# Revit family: Grohe_ThermostaticShowerMixer_34827KF0
name_source: partatom
category: Plumbing Fixtures
units: mm (PartAtom-declared; Revit-internal decimal feet)

## family parameters
Cut with Voids When Loaded = No
Host = Face
OmniClass Number = 23.45.05.00
OmniClass Title = Sanitary Equipment
Part Type = Normal
Room Calculation Point = No
Round Connector Dimension = Use Diameter
Shared = No

## types (1)
- Thermostatic Shower Mixer (34827KF0)
    Assembly Code = D2013
    AssetType = Fixed
    BIMObjectName = Grohe_ThermostaticShowerMixer_34827KF0
    CO2NeutralProduction = GROHE is one of the first leading manufacturer within the sanitary industry having a CO2-neutral production.
    ClassificationName = Uniclass2015
    ClassificationValue = Pr_40_20_87_55
    Color = Grohe_Black
    Cost = 0 $
    Default Elevation = 0 mm  [stored 0 ft]
    Description = Thermostatic Shower Mixer
    DimensionsDocumentLink = https://cdn.cloud.grohe.com
    DocumentationCertificates = https://www.bimstore.co
    DocumentationInstallationGuide = https://www.bimstore.co
    DocumentationLiterature = https://www.bimstore.co
    DocumentationMaintenance = https://www.bimstore.co
    DocumentationTechnical = https://www.bimstore.co
    DurationUnit = Years
    Ecojoy = No
    ExpectedLife = 0
    Finish = Black
    FullRecyclabilityOfPlastic = All plastic components are fully recycable
    GROHESocialCommittment = green.grohe.com/social_engagement
    GROHESustainability = green.grohe.com
    IfcExportAs = IfcPipeFitting
    IfcExportType = IfcPipeFittingType
    Keynote = N16
    Manufacturer = Grohe
    ManufacturerName = Grohe
    Model = Thermostatic Shower Mixer
    ModelNumber = 34827KF0
    ModelReference = Thermostatic Shower Mixer
    NBSDescription = Shower fittings package
    NBSObjectName = Grohe - Shower fittings package
    NBSReference = 45-35-70/323
    NominalDepth = 0 mm  [stored 0 ft]
    NominalHeight = 0 mm  [stored 0 ft]
    NominalLength = 0 mm  [stored 0 ft]
    PQDiagramLink = https://cdn.cloud.grohe.com
    PrimaryMaterial = Grohe_Black
    ProductDescription = wall mounted

GROHE CoolTouch safety housing

GROHE Long-Life finish

GROHE SafeStop safety button at 38°C

GROHE SafeStop Plus optional temperature limiter at 43°C included

GROHE TurboStat compact cartridge with wax thermoelement

GROHE ProGrip with knurl structure

integrated mixed water shut off

volume handle with GROHE EcoButton (economy button with individually adjustable economy stop)

ceramic headpart 1/2", 180°

shower bottom outlet 1/2"

built-in non return valves

dirt strainers

protected against backflow

S-unions

metal escutcheon

GROHE Water Saving - Less water, perfect flow

professional exclusive
    ProductNumber = 34827KF0
    ProductShortText = Thermostatic shower mixer 1/2"
    ProductType = Thermostat
    ProductionYear = 2023
    SustainabilityAward = green.grohe.com/awards
    SustainabilityReport = green.grohe.com/reporting
    TPIDocumentLink = https://cdn.cloud.grohe.com
    Type Comments = Thermostatic Shower Mixer
    TypeName = Thermostatic Shower Mixer
    URL = https://www.grohe.co.uk
    WarrantyDurationLabor = 0
    WarrantyDurationParts = 0
    WarrantyDurationUnit = Years
    _BSBibleVersion = 17
    _BimSpecGuid = 0
    _CurrentRevision = 1
    _DistributedBy = https://www.bimstore.co
    _ObjectUserGuide = https://www.bimstore.co

note: [stored X ft] marks values corroborated as IEEE doubles in the binary element streams (Revit-internal decimal feet)

## geometry (parser evidence)
native form markers: Sweep x2
no freeform markers — native parametric forms only
